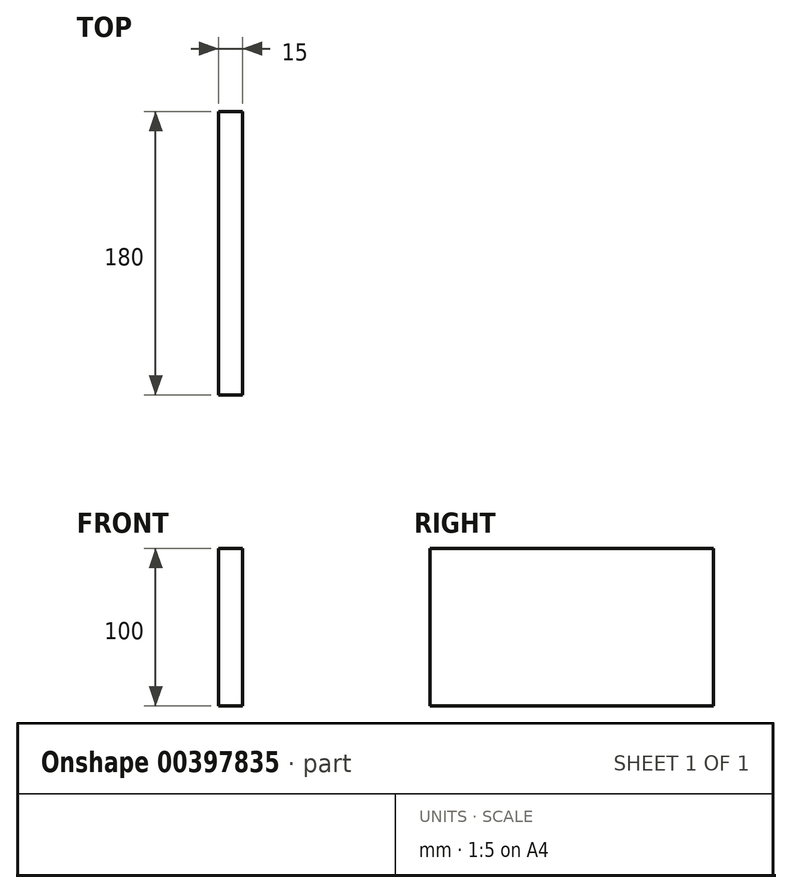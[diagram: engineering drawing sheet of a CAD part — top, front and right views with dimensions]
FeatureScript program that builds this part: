
annotation { "Feature Type Name" : "Feature", "Feature Type Description" : "" }
export const myFeature = defineFeature(function(context is Context, id is Id, definition is map)
    precondition{}
    {
        {
            var Q0;
            Q0=qCreatedBy(makeId("Top.planeOp"),FACE);
            var sketch = newSketch(context, id + "F0", { "sketchPlane" : qUnion([Q0])});
            skLineSegment(sketch, "E0.bottom", {"start": v(7.5, 90) * mm, "end": v(-7.5, 90) * mm});
            skLineSegment(sketch, "E0.top", {"start": v(7.5, -90) * mm, "end": v(-7.5, -90) * mm});
            skLineSegment(sketch, "E0.left", {"start": v(7.5, 90) * mm, "end": v(7.5, -90) * mm});
            skLineSegment(sketch, "E0.right", {"start": v(-7.5, 90) * mm, "end": v(-7.5, -90) * mm});
            skPoint(sketch, "E0.middle", {"position": v(0, 0) * mm});
            skSolve(sketch);
        }
        {
            var Q0;
            Q0 = qSketchRegion(id + "F0", true);
            extrude(context, id + "F1", {"entities" : qUnion([Q0]), "depth" : 100 * mm});
        }
    });
